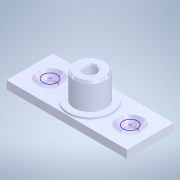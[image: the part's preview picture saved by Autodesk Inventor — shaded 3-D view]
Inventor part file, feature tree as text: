
AUTODESK INVENTOR PART (.ipt)
format: ipt  version: 2021 (Build 250183000, 183)  size: 166,400 bytes
history: native  units: in
note: dims shown in document units (in); Inventor stores cm internally (conversion verified against a paired STEP export)
features: sketch x5, extrude x3, chamfer x2, hole x1, projected_geometry x1, other x1
ambient origin geometry x8: Origin, YZ Plane, XZ Plane, XY Plane, X Axis, Y Axis, Z Axis, Center Point
bodies: Solid1 (feature_tree)
feature tree (13):
  extrude  "Extrusion1"  Depth=0.3937in TaperAngle=0.0deg
  extrude  "Extrusion2"  Depth=0.3937in TaperAngle=0.0deg
  extrude  "Extrusion3"  Depth=0.002in
  chamfer  "Chamfer1"  Distance=0.0118in Angle=45.0deg
  sketch  "Sketch4"  dims[d19=0.1339in d20=0.2362in d21=0.248in d22=0.0787in d23=90.0deg d24=0.315in d25=0.0in d26=0.002in]
  hole  "Hole2"  [1 undecoded]
  chamfer  "Chamfer2"  [1 undecoded]
  sketch  "Sketch1"  dims[d1=0.3937in d2=0.0in d3=0.3937in d4=0.0in]
  projected_geometry  "Projected Loop1"
  sketch  "Sketch2"  dims[d5=0.0039in d6=0.3937in d7=0.0in]
  sketch  "Sketch3"  dims[d8=0.0197in d9=0.0787in d10=45.0deg]
  sketch  "Sketch6"  dims[d27=0.002in d28=0.0118in d29=0.0787in d30=45.0deg]
  other  "CSK for M4 Countersunk Flat Head Screw1"
note: 2 required parameter values undecoded (feature->parameter linkage not recoverable at this tier; creation-order binding heuristic only, values carry confidence <= 0.55)
